# Revit family: OPERLUX
name_source: partatom
category: Осветительные приборы
units: mm (PartAtom-declared; Revit-internal decimal feet)

## family parameters
Всегда вертикально = Нет
Источник света = Да
На основе рабочей плоскости = Нет
Общий = Нет
При загрузке вырезать с полостями = Нет
Размер круглого соединителя = Использовать диаметр
Тип детали = Нормальный
Точка расчета площади = Да

## types (8) — shared parameters
ADSK_Единица измерения = шт.
ADSK_Завод-изготовитель = ЗАО «Центрстройсвет»
ADSK_Классификация нагрузок = Прочее
ADSK_Количество фаз = 1
ADSK_Количество фаз числовое = 1
ADSK_Коэффициент мощности = 0.92
ADSK_Масса = 4.2
ADSK_Напряжение = 230 В
ADSK_Ток = 0 А
URL = http://csvt.ru
Видимая форма излучения при визуализации = Да
Высота = 80 мм
Длина = 588 мм
Изготовитель = ЗАО «Центрстройсвет»
Излучение по длине прямоугольника = 548 мм
Излучение по ширине прямоугольника = 548 мм
Материал коробки = RAL 9006
Материал светильника = RAL 9001
Материал стекла = RAL светящийся
Светофильтр = 16777215
Смещение цветовой температуры при затухании лампы = <Нет>
Угол наклона = 90.00°
Ширина = 588 мм
Ширина корпуса = 607 мм

## per-type parameters (varying)
| type | ADSK_Код изделия | ADSK_Наименование | ADSK_Номинальная мощность | ADSK_Обозначение | ADSK_Полная мощность | Файл фотометрической сетки |
| CSVT Operlux - 34/opal-sand (IP20, 4000К, грильято) | ЦБ000007880 | Встраиваемый светодиодный светильник CSVT Operlux-34/opal-sand (IP20, 4000К, грильято) | 32 Вт | CSVT Operlux-34/opal-sand (IP20, 4000К, грильято) | 35 В·А | Светильник OPERLUX-34 PRISMA-(588x588).IES |
| CSVT Operlux - 34/opal-sand (IP20, 4000К, грильято) с БАП на 1 час | ЦБ000007881 | Встраиваемый светодиодный светильник CSVT Operlux-34/opal-sand (IP20, 4000К, грильято) с БАП на 1 час | 32 Вт | CSVT Operlux-34/opal-sand (IP20, 4000К, грильято) | 35 В·А | Светильник OPERLUX-34 PRISMA-(588x588).IES |
| CSVT Operlux - 34/opal-sand (IP20, 4000К, грильято) с БАП на 3 часа | ЦБ000007882 | Встраиваемый светодиодный светильник CSVT Operlux-34/opal-sand (IP20, 4000К, грильято) с БАП на 3 часа | 32 Вт | CSVT Operlux-34/opal-sand (IP20, 4000К, грильято) | 35 В·А | Светильник OPERLUX-34 PRISMA-(588x588).IES |
| CSVT Operlux - 50/opal-sand (IP20, 4000К, грильято) | ЦБ000007888 | Встраиваемый светодиодный светильник CSVT Operlux-50/opal-sand (IP20, 4000К, грильято) | 48 Вт | CSVT Operlux-50/opal-sand (IP20, 4000К, грильято) | 52 В·А | Светильник OPERLUX-50 OPAL-SAND-(595х595).IES |
| CSVT Operlux-34/prisma  (IP20, 4000К, грильято) | ЦБ000006714 | Встраиваемый светодиодный светильник CSVT Operlux-34/prisma  (IP20, 4000К, грильято) | 32 Вт | CSVT Operlux-34/prisma  (IP20, 4000К, грильято) | 35 В·А | Светильник OPERLUX-34 PRISMA-(588x588).IES |
| CSVT Operlux-34/prisma  (IP20, 4000К, грильято) c БАП на 1 час. | ЦБ000006771 | Встраиваемый светодиодный светильник CSVT Operlux-34/prisma  (IP20, 4000К, грильято) c БАП на 1 час. | 32 Вт | CSVT Operlux-34/prisma  (IP20, 4000К, грильято) | 35 В·А | Светильник OPERLUX-34 PRISMA-(588x588).IES |
| CSVT Operlux-34/prisma  (IP20, 4000К, грильято) c БАП на 3 час. | ЦБ000006770 | Встраиваемый светодиодный светильник CSVT Operlux-34/prisma  (IP20, 4000К, грильято) c БАП на 3 час. | 32 Вт | CSVT Operlux-34/prisma  (IP20, 4000К, грильято) | 35 В·А | Светильник OPERLUX-34 PRISMA-(588x588).IES |
| CSVT Operlux-50/prisma  (IP20, 4000К, грильято) | ЦБ000008093 | Встраиваемый светодиодный светильник CSVT Operlux-50/prisma  (IP20, 4000К, грильято) | 48 Вт | CSVT Operlux-50/prisma  (IP20, 4000К, грильято) | 52 В·А | Светильник OPERLUX-50 PRISMA-(595х595).IES |
